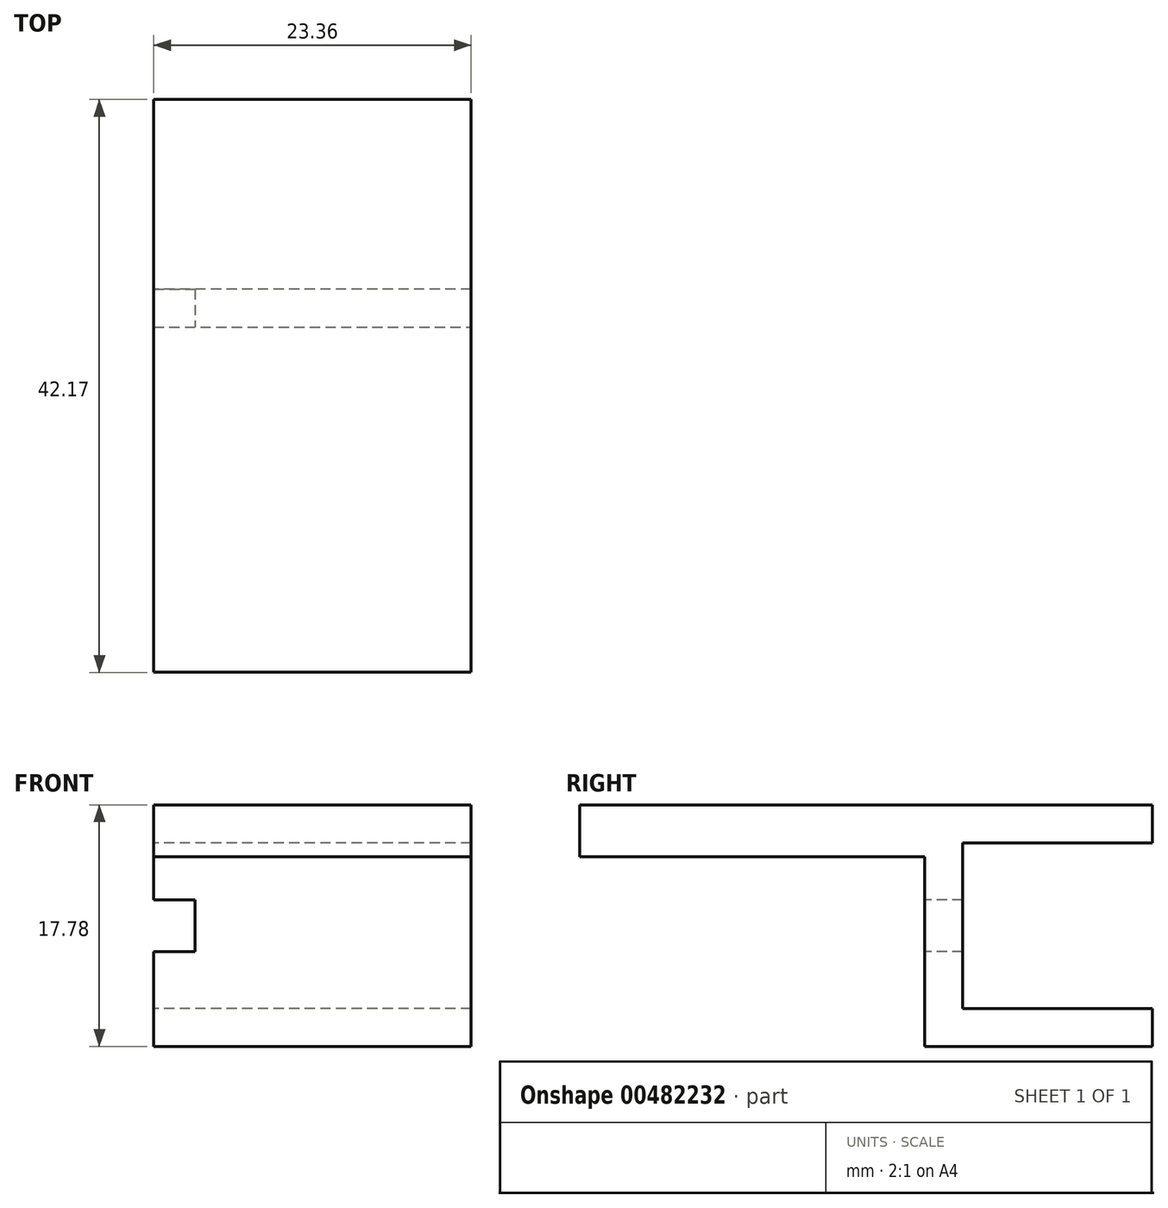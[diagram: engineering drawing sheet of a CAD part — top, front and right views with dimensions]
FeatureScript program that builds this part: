
annotation { "Feature Type Name" : "Feature", "Feature Type Description" : "" }
export const myFeature = defineFeature(function(context is Context, id is Id, definition is map)
    precondition{}
    {
        {
            var Q0;
            Q0=qCreatedBy(makeId("Top.planeOp"),FACE);
            var sketch = newSketch(context, id + "F0", { "sketchPlane" : qUnion([Q0])});
            skLineSegment(sketch, "E0.bottom", {"start": v(11.68, -6.99) * mm, "end": v(-11.68, -6.99) * mm});
            skLineSegment(sketch, "E0.top", {"start": v(11.68, 6.99) * mm, "end": v(-11.68, 6.99) * mm});
            skLineSegment(sketch, "E0.left", {"start": v(11.68, -6.99) * mm, "end": v(11.68, 6.99) * mm});
            skLineSegment(sketch, "E0.right", {"start": v(-11.68, -6.99) * mm, "end": v(-11.68, 6.99) * mm});
            skPoint(sketch, "E0.middle", {"position": v(0, 0) * mm});
            skSolve(sketch);
        }
        {
            var Q0;
            Q0=makeQuery(id+"F0.imprint","IMPRINT",FACE,{"disambiguationData":[TD([[makeQuery(id+"F0.imprint","IMPRINT",EDGE,{"derivedFrom":sQuery(id+"F0.wireOp",EDGE,"E0.bottom")}),-1.0]])]});
            extrude(context, id + "F1", {"entities" : qUnion([Q0]), "depth" : 2.8 * mm, "offsetDistance" : 25.4 * mm});
        }
        {
            var Q0;
            Q0=makeQuery(id+"F1.opExtrude","CAP_FACE",FACE,{"disambiguationData":[OSD([sQuery(id+"F0.wireOp",EDGE,"E0.bottom"),sQuery(id+"F0.wireOp",EDGE,"E0.top"),sQuery(id+"F0.wireOp",EDGE,"E0.left"),sQuery(id+"F0.wireOp",EDGE,"E0.right")])],"isStart":true});
            var sketch = newSketch(context, id + "F2", { "sketchPlane" : qUnion([Q0])});
            skLineSegment(sketch, "E1.bottom", {"start": v(11.68, 6.99) * mm, "end": v(-11.68, 6.99) * mm});
            skLineSegment(sketch, "E1.top", {"start": v(11.68, 9.78) * mm, "end": v(-11.68, 9.78) * mm});
            skLineSegment(sketch, "E1.left", {"start": v(11.68, 6.99) * mm, "end": v(11.68, 9.78) * mm});
            skLineSegment(sketch, "E1.right", {"start": v(-11.68, 6.99) * mm, "end": v(-11.68, 9.78) * mm});
            skPoint(sketch, "E1.middle", {"position": v(0, 8.38) * mm});
            skSolve(sketch);
        }
        {
            var Q0;
            Q0=makeQuery(id+"F2.imprint","IMPRINT",FACE,{"disambiguationData":[TD([[makeQuery(id+"F2.imprint","IMPRINT",EDGE,{"derivedFrom":sQuery(id+"F2.wireOp",EDGE,"E1.bottom")}),-1.0]])]});
            extrude(context, id + "F3", {"entities" : qUnion([Q0]), "operationType" : NewBodyOperationType.ADD, "oppositeDirection" : true, "depth" : 15 * mm, "offsetDistance" : 25.4 * mm});
        }
        {
            var Q0;
            Q0=makeQuery(id+"F3.opExtrude","CAP_FACE",FACE,{"disambiguationData":[OSD([sQuery(id+"F2.wireOp",EDGE,"E1.bottom"),sQuery(id+"F2.wireOp",EDGE,"E1.top"),sQuery(id+"F2.wireOp",EDGE,"E1.left"),sQuery(id+"F2.wireOp",EDGE,"E1.right")])],"isStart":false});
            extrude(context, id + "F4", {"entities" : qUnion([Q0]), "operationType" : NewBodyOperationType.ADD, "depth" : 2.8 * mm, "offsetDistance" : 25.4 * mm});
        }
        {
            var Q0;
            {var subQ0=sQuery(id+"F2.wireOp",EDGE,"E1.bottom");Q0=makeQuery(id+"F4.boolean.opBoolean","MERGE",FACE,{"derivedFrom":[makeQuery(id+"F3.opExtrude","SWEPT_FACE",FACE,{"disambiguationData":[OSD([subQ0])]}),makeQuery(id+"F4.opExtrude","SWEPT_FACE",FACE,{"disambiguationData":[OSD([subQ0])]})]});}
            var sketch = newSketch(context, id + "F5", { "sketchPlane" : qUnion([Q0])});
            skLineSegment(sketch, "E2.bottom", {"start": v(-11.68, 17.78) * mm, "end": v(11.68, 17.78) * mm});
            skLineSegment(sketch, "E2.top", {"start": v(-11.68, 14.99) * mm, "end": v(11.68, 14.99) * mm});
            skLineSegment(sketch, "E2.left", {"start": v(-11.68, 17.78) * mm, "end": v(-11.68, 14.99) * mm});
            skLineSegment(sketch, "E2.right", {"start": v(11.68, 17.78) * mm, "end": v(11.68, 14.99) * mm});
            skSolve(sketch);
        }
        {
            var Q0;
            Q0=makeQuery(id+"F5.imprint","IMPRINT",FACE,{"disambiguationData":[TD([[makeQuery(id+"F5.imprint","IMPRINT",EDGE,{"derivedFrom":sQuery(id+"F5.wireOp",EDGE,"E2.bottom")}),-1.0]])]});
            extrude(context, id + "F6", {"entities" : qUnion([Q0]), "operationType" : NewBodyOperationType.ADD, "depth" : 13.97 * mm, "offsetDistance" : 25.4 * mm});
        }
        {
            var Q0;
            {var subQ0=sQuery(id+"F2.wireOp",EDGE,"E1.top");Q0=makeQuery(id+"F4.boolean.opBoolean","MERGE",FACE,{"derivedFrom":[makeQuery(id+"F3.opExtrude","SWEPT_FACE",FACE,{"disambiguationData":[OSD([subQ0])]}),makeQuery(id+"F4.opExtrude","SWEPT_FACE",FACE,{"disambiguationData":[OSD([subQ0])]})]});}
            var sketch = newSketch(context, id + "F7", { "sketchPlane" : qUnion([Q0])});
            skLineSegment(sketch, "E3.bottom", {"start": v(-11.68, 10.8) * mm, "end": v(-8.64, 10.8) * mm});
            skLineSegment(sketch, "E3.top", {"start": v(-11.68, 6.99) * mm, "end": v(-8.64, 6.99) * mm});
            skLineSegment(sketch, "E3.left", {"start": v(-11.68, 10.8) * mm, "end": v(-11.68, 6.99) * mm});
            skLineSegment(sketch, "E3.right", {"start": v(-8.64, 10.8) * mm, "end": v(-8.64, 6.99) * mm});
            skLineSegment(sketch, "E4", {"start": v(-11.68, 17.78) * mm, "end": v(-11.68, 8.9) * mm});
            skSolve(sketch);
        }
        {
            var Q0;
            {var subQ1=sQuery(id+"F7.wireOp",EDGE,"E3.bottom");Q0=makeQuery(id+"F7.imprint","IMPRINT",FACE,{"disambiguationData":[TD([[makeQuery(id+"F7.imprint","IMPRINT",EDGE,{"derivedFrom":subQ1}),-1.0]])]});}
            extrude(context, id + "F8", {"entities" : qUnion([Q0]), "operationType" : NewBodyOperationType.REMOVE, "oppositeDirection" : true, "depth" : 25.4 * mm, "offsetDistance" : 25.4 * mm});
        }
        {
            var Q0;
            {var subQ0=sQuery(id+"F2.wireOp",EDGE,"E1.top");Q0=makeQuery(id+"F4.boolean.opBoolean","MERGE",FACE,{"derivedFrom":[makeQuery(id+"F3.opExtrude","SWEPT_FACE",FACE,{"disambiguationData":[OSD([subQ0])]}),makeQuery(id+"F4.opExtrude","SWEPT_FACE",FACE,{"disambiguationData":[OSD([subQ0])]})]});}
            var sketch = newSketch(context, id + "F9", { "sketchPlane" : qUnion([Q0])});
            skLineSegment(sketch, "E5.bottom", {"start": v(-11.68, 17.78) * mm, "end": v(11.68, 17.78) * mm});
            skLineSegment(sketch, "E5.top", {"start": v(-11.68, 13.97) * mm, "end": v(11.68, 13.97) * mm});
            skLineSegment(sketch, "E5.left", {"start": v(-11.68, 17.78) * mm, "end": v(-11.68, 13.97) * mm});
            skLineSegment(sketch, "E5.right", {"start": v(11.68, 17.78) * mm, "end": v(11.68, 13.97) * mm});
            skSolve(sketch);
        }
        {
            var Q0;
            Q0=makeQuery(id+"F9.imprint","IMPRINT",FACE,{"disambiguationData":[TD([[makeQuery(id+"F9.imprint","IMPRINT",EDGE,{"derivedFrom":sQuery(id+"F9.wireOp",EDGE,"E5.bottom")}),1.0]])]});
            extrude(context, id + "F10", {"entities" : qUnion([Q0]), "operationType" : NewBodyOperationType.ADD, "depth" : 25.4 * mm, "offsetDistance" : 25.4 * mm});
        }
    });
